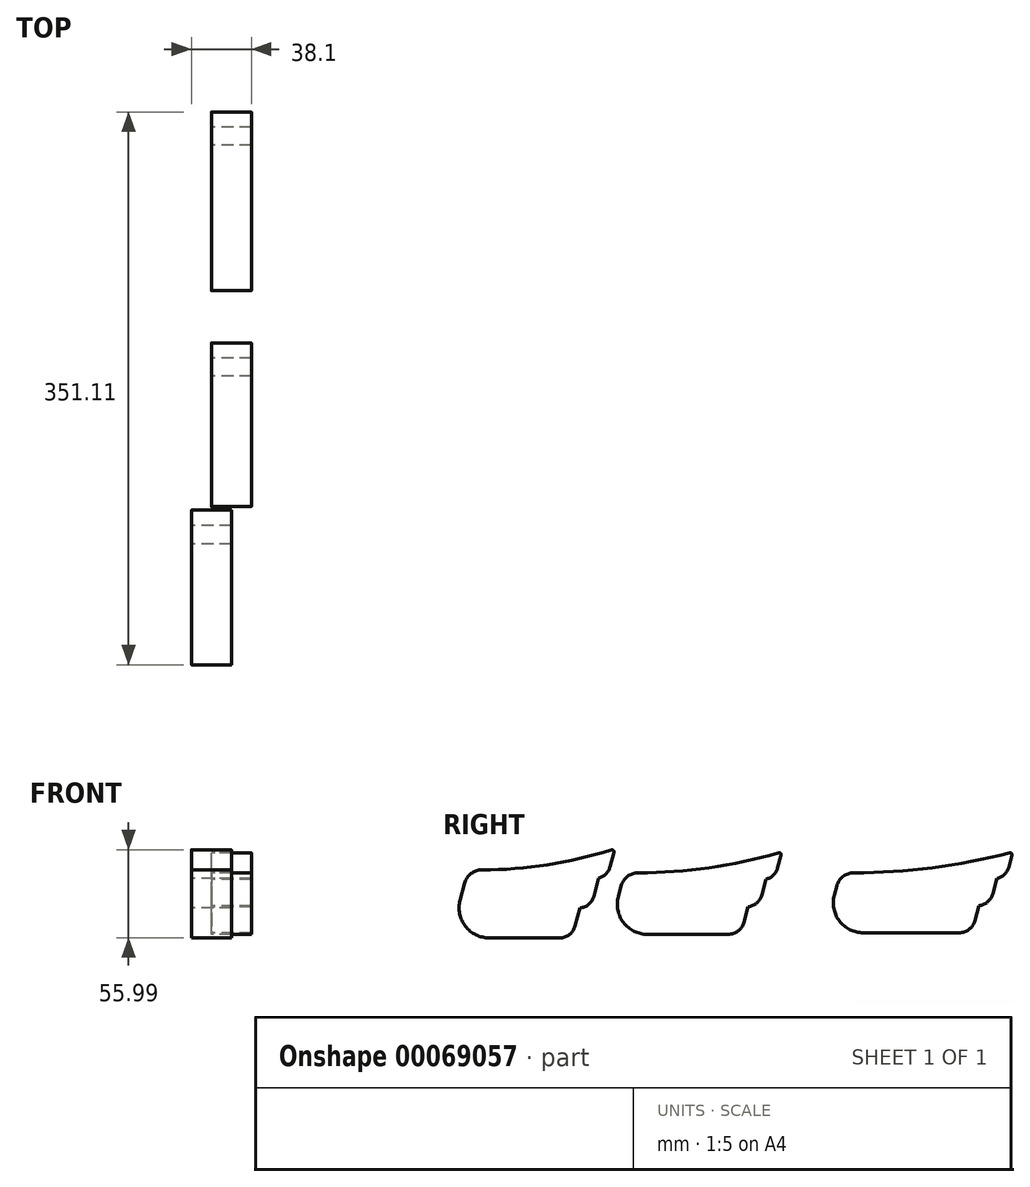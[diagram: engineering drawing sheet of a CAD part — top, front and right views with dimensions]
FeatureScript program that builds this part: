
annotation { "Feature Type Name" : "Feature", "Feature Type Description" : "" }
export const myFeature = defineFeature(function(context is Context, id is Id, definition is map)
    precondition{}
    {
        {
            var Q0;
            Q0=qCreatedBy(makeId("Right.planeOp"),FACE);
            var sketch = newSketch(context, id + "F0", { "sketchPlane" : qUnion([Q0])});
            skLineSegment(sketch, "E0.bottom", {"start": v(-30.48, 16.5) * mm, "end": v(30.48, 16.5) * mm, "construction": true});
            skLineSegment(sketch, "E0.top", {"start": v(-30.48, -16.51) * mm, "end": v(30.48, -16.51) * mm, "construction": true});
            skLineSegment(sketch, "E0.left", {"start": v(-30.48, 16.5) * mm, "end": v(-30.48, -16.5) * mm, "construction": true});
            skLineSegment(sketch, "E0.right", {"start": v(30.48, 16.51) * mm, "end": v(30.48, -16.51) * mm, "construction": true});
            skLineSegment(sketch, "E1", {"start": v(-36.1, 12.42) * mm, "end": v(-39, 1.64) * mm});
            skLineSegment(sketch, "E2", {"start": v(-20.6, -22.34) * mm, "end": v(24.21, -22.34) * mm});
            skLineSegment(sketch, "E3", {"start": v(34.03, -14.8) * mm, "end": v(37.1, -3.33) * mm});
            skLineSegment(sketch, "E4", {"start": v(45.88, 4.15) * mm, "end": v(48.95, 15.63) * mm});
            skLineSegment(sketch, "E5", {"start": v(56.14, 22.81) * mm, "end": v(58.62, 32.05) * mm});
            skArc(sketch, "E6.filletArc", {"start": v(-39, 1.64) * mm, "mid": v(-35.7, -14.88) * mm, "end": v(-20.6, -22.34) * mm});
            skArc(sketch, "E7.filletArc", {"start": v(-25.07, 20.89) * mm, "mid": v(-32.03, 18.53) * mm, "end": v(-36.1, 12.42) * mm});
            skLineSegment(sketch, "E8", {"start": v(-30.48, 16.5) * mm, "end": v(-25.07, 20.89) * mm, "construction": true});
            skLineSegment(sketch, "E9", {"start": v(-30.48, 16.51) * mm, "end": v(-36.1, 12.42) * mm, "construction": true});
            skArc(sketch, "E10.filletArc", {"start": v(24.21, -22.34) * mm, "mid": v(30.4, -20.24) * mm, "end": v(34.03, -14.8) * mm});
            skArc(sketch, "E11.filletArc", {"start": v(37.1, -3.33) * mm, "mid": v(42.65, -0.96) * mm, "end": v(45.88, 4.15) * mm});
            skArc(sketch, "E12.filletArc", {"start": v(48.95, 15.63) * mm, "mid": v(53.51, 18.25) * mm, "end": v(56.14, 22.81) * mm});
            skArc(sketch, "E13.filletArc", {"start": v(58.62, 32.05) * mm, "mid": v(58.27, 33.3) * mm, "end": v(57, 33.59) * mm});
            skArc(sketch, "E14", {"start": v(57, 33.59) * mm, "mid": v(16.46, 24.08) * mm, "end": v(-25.07, 20.89) * mm});
            skLineSegment(sketch, "E15", {"start": v(57, 33.59) * mm, "end": v(59.22, 34.29) * mm, "construction": true});
            skLineSegment(sketch, "E16", {"start": v(59.22, 34.29) * mm, "end": v(56.14, 22.81) * mm, "construction": true});
            skLineSegment(sketch, "E17", {"start": v(45.08, 30.1) * mm, "end": v(48.95, 15.63) * mm, "construction": true});
            skLineSegment(sketch, "E18", {"start": v(30.8, 26.7) * mm, "end": v(37.1, -3.33) * mm, "construction": true});
            skPoint(sketch, "E19", {"position": v(0, 0) * mm});
            skPoint(sketch, "E19.positionSnap0", {"position": v(-30.48, 0) * mm});
            skPoint(sketch, "E19.positionSnap1", {"position": v(0, -16.5) * mm});
            skLineSegment(sketch, "E20", {"start": v(-25.07, 20.89) * mm, "end": v(0, 20.89) * mm, "construction": true});
            skLineSegment(sketch, "E21", {"start": v(37.1, -3.33) * mm, "end": v(37.1, 28.1) * mm, "construction": true});
            skLineSegment(sketch, "E22", {"start": v(30.8, 26.7) * mm, "end": v(37.1, 28.1) * mm, "construction": true});
            skLineSegment(sketch, "E23", {"start": v(33.95, 27.4) * mm, "end": v(37.1, -3.33) * mm, "construction": true});
            skSolve(sketch);
        }
        {
            var Q0;
            Q0 = qSketchRegion(id + "F0", true);
            extrude(context, id + "F1", {"entities" : qUnion([Q0]), "endBound" : BoundingType.SYMMETRIC, "depth" : 25.4 * mm});
        }
        {
            var Q0;
            Q0=qCreatedBy(makeId("Right.planeOp"),FACE);
            var sketch = newSketch(context, id + "F2", { "sketchPlane" : qUnion([Q0])});
            skLineSegment(sketch, "E24.bottom", {"start": v(-30.48, 16.5) * mm, "end": v(30.48, 16.5) * mm, "construction": true});
            skLineSegment(sketch, "E24.top", {"start": v(-30.48, -16.51) * mm, "end": v(30.48, -16.51) * mm, "construction": true});
            skLineSegment(sketch, "E24.left", {"start": v(-30.48, 16.5) * mm, "end": v(-30.48, -16.5) * mm, "construction": true});
            skLineSegment(sketch, "E24.right", {"start": v(30.48, 16.5) * mm, "end": v(30.48, -16.5) * mm, "construction": true});
            skLineSegment(sketch, "E25", {"start": v(-47.37, 10.58) * mm, "end": v(-48.88, 4.93) * mm});
            skLineSegment(sketch, "E26", {"start": v(-30.48, -19.05) * mm, "end": v(30.48, -19.05) * mm});
            skLineSegment(sketch, "E27", {"start": v(40.3, -11.52) * mm, "end": v(42.89, -1.83) * mm});
            skLineSegment(sketch, "E28", {"start": v(51.75, 5.65) * mm, "end": v(54.34, 15.34) * mm});
            skLineSegment(sketch, "E29", {"start": v(61.88, 22.61) * mm, "end": v(63.9, 30.2) * mm});
            skArc(sketch, "E30.filletArc", {"start": v(-48.88, 4.93) * mm, "mid": v(-45.6, -11.6) * mm, "end": v(-30.48, -19.05) * mm});
            skArc(sketch, "E31.filletArc", {"start": v(-36.33, 19.05) * mm, "mid": v(-43.29, 16.69) * mm, "end": v(-47.37, 10.58) * mm});
            skLineSegment(sketch, "E32", {"start": v(-30.48, 16.5) * mm, "end": v(-36.33, 19.05) * mm, "construction": true});
            skLineSegment(sketch, "E33", {"start": v(-30.48, 16.5) * mm, "end": v(-47.37, 10.58) * mm, "construction": true});
            skArc(sketch, "E34.filletArc", {"start": v(30.48, -19.05) * mm, "mid": v(36.67, -16.95) * mm, "end": v(40.3, -11.52) * mm});
            skArc(sketch, "E35.filletArc", {"start": v(42.89, -1.83) * mm, "mid": v(48.5, 0.52) * mm, "end": v(51.75, 5.65) * mm});
            skArc(sketch, "E36.filletArc", {"start": v(54.34, 15.34) * mm, "mid": v(59.12, 17.93) * mm, "end": v(61.88, 22.61) * mm});
            skArc(sketch, "E37.filletArc", {"start": v(63.9, 30.2) * mm, "mid": v(63.58, 31.42) * mm, "end": v(62.36, 31.75) * mm});
            skArc(sketch, "E38", {"start": v(62.36, 31.75) * mm, "mid": v(13.42, 22.24) * mm, "end": v(-36.33, 19.05) * mm});
            skLineSegment(sketch, "E39", {"start": v(62.36, 31.75) * mm, "end": v(64.47, 32.3) * mm, "construction": true});
            skLineSegment(sketch, "E40", {"start": v(64.47, 32.3) * mm, "end": v(61.88, 22.61) * mm, "construction": true});
            skLineSegment(sketch, "E41", {"start": v(51.2, 29) * mm, "end": v(54.34, 15.34) * mm, "construction": true});
            skLineSegment(sketch, "E42", {"start": v(37.5, 26.1) * mm, "end": v(42.89, -1.83) * mm, "construction": true});
            skPoint(sketch, "E43", {"position": v(0, 0) * mm});
            skPoint(sketch, "E43.positionSnap1", {"position": v(0, -16.51) * mm});
            skLineSegment(sketch, "E44", {"start": v(-36.33, 19.05) * mm, "end": v(0, 19.05) * mm, "construction": true});
            skLineSegment(sketch, "E45", {"start": v(42.89, -1.83) * mm, "end": v(42.89, 27.19) * mm, "construction": true});
            skLineSegment(sketch, "E46", {"start": v(37.5, 26.1) * mm, "end": v(42.89, 27.19) * mm, "construction": true});
            skLineSegment(sketch, "E47", {"start": v(40.2, 26.65) * mm, "end": v(42.89, -1.83) * mm, "construction": true});
            skSolve(sketch);
        }
        {
            var Q0;
            Q0=makeQuery(id+"F2.imprint","IMPRINT",FACE,{"disambiguationData":[TD([[makeQuery(id+"F2.imprint","IMPRINT",EDGE,{"derivedFrom":sQuery(id+"F2.wireOp",EDGE,"E25")}),1.0]])]});
            extrude(context, id + "F3", {"entities" : qUnion([Q0]), "depth" : 25.4 * mm});
        }
        {
            var Q0;
            Q0=qCreatedBy(makeId("Right.planeOp"),FACE);
            var sketch = newSketch(context, id + "F4", { "sketchPlane" : qUnion([Q0])});
            skLineSegment(sketch, "E48.bottom", {"start": v(-30.48, 16.51) * mm, "end": v(30.48, 16.51) * mm, "construction": true});
            skLineSegment(sketch, "E48.top", {"start": v(-30.48, -16.5) * mm, "end": v(30.48, -16.5) * mm, "construction": true});
            skLineSegment(sketch, "E48.left", {"start": v(-30.48, 16.5) * mm, "end": v(-30.48, -16.5) * mm, "construction": true});
            skLineSegment(sketch, "E48.right", {"start": v(30.48, 16.5) * mm, "end": v(30.48, -16.5) * mm, "construction": true});
            skLineSegment(sketch, "E49", {"start": v(-41.4, 10.58) * mm, "end": v(-43.18, 3.91) * mm});
            skLineSegment(sketch, "E50", {"start": v(-24.78, -20.07) * mm, "end": v(26.68, -20.07) * mm});
            skLineSegment(sketch, "E51", {"start": v(36.5, -12.54) * mm, "end": v(39.16, -2.58) * mm});
            skLineSegment(sketch, "E52", {"start": v(47.96, 4.9) * mm, "end": v(50.64, 14.9) * mm});
            skLineSegment(sketch, "E53", {"start": v(57.97, 22.12) * mm, "end": v(60.14, 30.2) * mm});
            skArc(sketch, "E54.filletArc", {"start": v(-43.18, 3.91) * mm, "mid": v(-39.9, -12.61) * mm, "end": v(-24.78, -20.07) * mm});
            skArc(sketch, "E55.filletArc", {"start": v(-30.35, 19.05) * mm, "mid": v(-37.31, 16.69) * mm, "end": v(-41.4, 10.58) * mm});
            skLineSegment(sketch, "E56", {"start": v(-30.48, 16.51) * mm, "end": v(-30.35, 19.05) * mm, "construction": true});
            skLineSegment(sketch, "E57", {"start": v(-30.48, 16.5) * mm, "end": v(-41.4, 10.58) * mm, "construction": true});
            skArc(sketch, "E58.filletArc", {"start": v(26.68, -20.07) * mm, "mid": v(32.86, -17.97) * mm, "end": v(36.5, -12.54) * mm});
            skArc(sketch, "E59.filletArc", {"start": v(39.16, -2.58) * mm, "mid": v(44.73, -0.22) * mm, "end": v(47.96, 4.9) * mm});
            skArc(sketch, "E60.filletArc", {"start": v(50.64, 14.9) * mm, "mid": v(55.29, 17.51) * mm, "end": v(57.97, 22.12) * mm});
            skArc(sketch, "E61.filletArc", {"start": v(60.14, 30.2) * mm, "mid": v(59.8, 31.44) * mm, "end": v(58.56, 31.75) * mm});
            skArc(sketch, "E62", {"start": v(58.56, 31.75) * mm, "mid": v(14.55, 22.24) * mm, "end": v(-30.35, 19.05) * mm});
            skLineSegment(sketch, "E63", {"start": v(58.56, 31.75) * mm, "end": v(60.72, 32.38) * mm, "construction": true});
            skLineSegment(sketch, "E64", {"start": v(47.18, 28.66) * mm, "end": v(50.64, 14.9) * mm, "construction": true});
            skLineSegment(sketch, "E65", {"start": v(33.4, 25.52) * mm, "end": v(39.16, -2.58) * mm, "construction": true});
            skPoint(sketch, "E66", {"position": v(0, 0) * mm});
            skPoint(sketch, "E66.positionSnap0", {"position": v(-30.48, 0) * mm});
            skPoint(sketch, "E66.positionSnap1", {"position": v(0, -16.51) * mm});
            skLineSegment(sketch, "E67", {"start": v(-30.35, 19.05) * mm, "end": v(0, 19.05) * mm, "construction": true});
            skLineSegment(sketch, "E68", {"start": v(39.16, -2.58) * mm, "end": v(39.16, 26.75) * mm, "construction": true});
            skLineSegment(sketch, "E69", {"start": v(33.4, 25.52) * mm, "end": v(39.16, 26.75) * mm, "construction": true});
            skLineSegment(sketch, "E70", {"start": v(36.28, 26.13) * mm, "end": v(39.16, -2.58) * mm, "construction": true});
            skLineSegment(sketch, "E71", {"start": v(60.72, 32.38) * mm, "end": v(56.04, 14.9) * mm, "construction": true});
            skLineSegment(sketch, "E72", {"start": v(50.64, 14.9) * mm, "end": v(45.96, -2.58) * mm, "construction": true});
            skLineSegment(sketch, "E73", {"start": v(39.16, -2.58) * mm, "end": v(34.47, -20.07) * mm, "construction": true});
            skSolve(sketch);
        }
        {
            var Q0;
            Q0=makeQuery(id+"F4.imprint","IMPRINT",FACE,{"disambiguationData":[TD([[makeQuery(id+"F4.imprint","IMPRINT",EDGE,{"derivedFrom":sQuery(id+"F4.wireOp",EDGE,"E49")}),1.0]])]});
            extrude(context, id + "F5", {"entities" : qUnion([Q0]), "depth" : 25.4 * mm});
        }
        {
            var Q0;
            Q0=makeQuery(id+"F1.opExtrude","SWEPT_BODY",BODY,{"disambiguationData":[OSD([sQuery(id+"F0.wireOp",EDGE,"E1"),sQuery(id+"F0.wireOp",EDGE,"E2"),sQuery(id+"F0.wireOp",EDGE,"E3"),sQuery(id+"F0.wireOp",EDGE,"E4"),sQuery(id+"F0.wireOp",EDGE,"E5"),sQuery(id+"F0.wireOp",EDGE,"E6.filletArc"),sQuery(id+"F0.wireOp",EDGE,"E7.filletArc"),sQuery(id+"F0.wireOp",EDGE,"E10.filletArc"),sQuery(id+"F0.wireOp",EDGE,"E11.filletArc"),sQuery(id+"F0.wireOp",EDGE,"E12.filletArc"),sQuery(id+"F0.wireOp",EDGE,"E13.filletArc"),sQuery(id+"F0.wireOp",EDGE,"E14")])]});
            transform(context, id + "F6", {"entities" : qUnion([Q0]), "transformType" : TransformType.TRANSLATION_3D, "dx" : 0 * mm, "dy" : -104.63 * mm, "dz" : 0 * mm, "makeCopy" : false});
        }
        {
            var Q0;
            Q0=makeQuery(id+"F3.opExtrude","SWEPT_BODY",BODY,{"disambiguationData":[OSD([sQuery(id+"F2.wireOp",EDGE,"E25"),sQuery(id+"F2.wireOp",EDGE,"E26"),sQuery(id+"F2.wireOp",EDGE,"E27"),sQuery(id+"F2.wireOp",EDGE,"E28"),sQuery(id+"F2.wireOp",EDGE,"E29"),sQuery(id+"F2.wireOp",EDGE,"E30.filletArc"),sQuery(id+"F2.wireOp",EDGE,"E31.filletArc"),sQuery(id+"F2.wireOp",EDGE,"E34.filletArc"),sQuery(id+"F2.wireOp",EDGE,"E35.filletArc"),sQuery(id+"F2.wireOp",EDGE,"E36.filletArc"),sQuery(id+"F2.wireOp",EDGE,"E37.filletArc"),sQuery(id+"F2.wireOp",EDGE,"E38")])]});
            transform(context, id + "F7", {"entities" : qUnion([Q0]), "transformType" : TransformType.TRANSLATION_3D, "dx" : 0 * mm, "dy" : 142.89 * mm, "dz" : 0 * mm, "makeCopy" : false});
        }
    });
